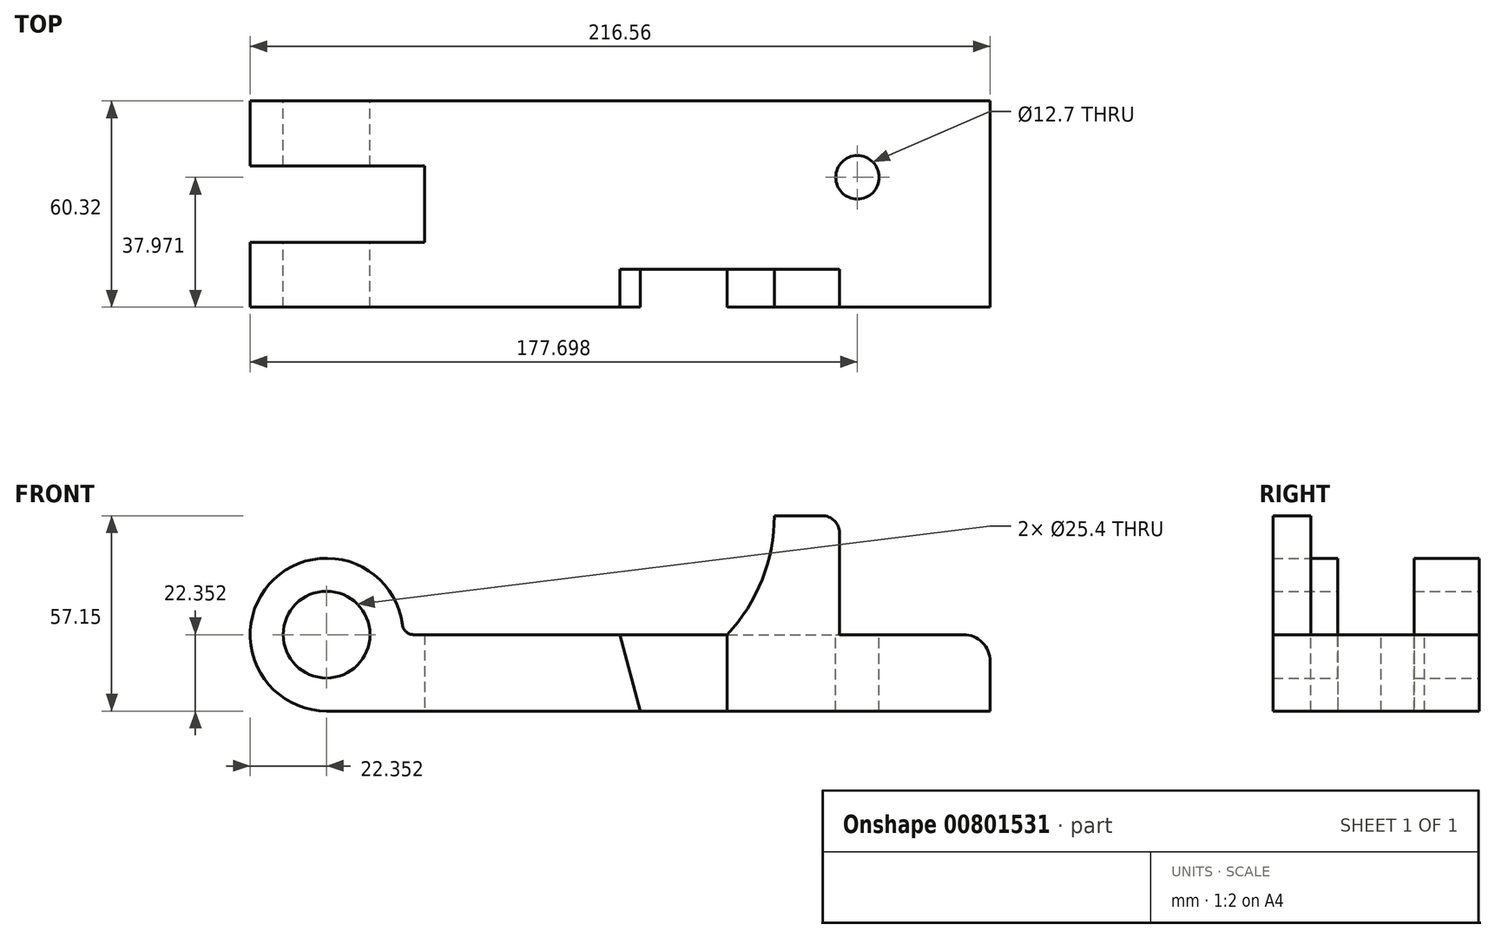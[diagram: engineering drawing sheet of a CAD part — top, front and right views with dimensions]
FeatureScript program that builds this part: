
annotation { "Feature Type Name" : "Feature", "Feature Type Description" : "" }
export const myFeature = defineFeature(function(context is Context, id is Id, definition is map)
    precondition{}
    {
        {
            var Q0;
            Q0=qCreatedBy(makeId("Front.planeOp"),FACE);
            var sketch = newSketch(context, id + "F0", { "sketchPlane" : qUnion([Q0])});
            skLineSegment(sketch, "E0.bottom", {"start": v(0, 0) * mm, "end": v(-194.2, 0) * mm});
            skLineSegment(sketch, "E0.top", {"start": v(-49.2, 57.15) * mm, "end": v(-63.17, 57.15) * mm});
            skLineSegment(sketch, "E0.left", {"start": v(0, 0) * mm, "end": v(0, 22.35) * mm});
            skLineSegment(sketch, "E1.bottom", {"start": v(-194.2, 0) * mm, "end": v(0, 0) * mm});
            skLineSegment(sketch, "E1.top", {"start": v(-216.56, 22.35) * mm, "end": v(-7.87, 22.35) * mm});
            skLineSegment(sketch, "E1.right", {"start": v(0, 0) * mm, "end": v(0, 14.48) * mm});
            skLineSegment(sketch, "E2", {"start": v(-76.96, 22.35) * mm, "end": v(-76.96, 0) * mm});
            skLineSegment(sketch, "E3", {"start": v(-194.2, 71.24) * mm, "end": v(-194.2, -42.33) * mm, "construction": true});
            skCircle(sketch, "E4", {"center": v(-194.2, 22.35) * mm, "radius": 12.7 * mm});
            skCircle(sketch, "E5", {"center": v(-194.2, 22.35) * mm, "radius": 22.35 * mm});
            skLineSegment(sketch, "E6", {"start": v(-102.36, 0) * mm, "end": v(-108.36, 22.35) * mm});
            skLineSegment(sketch, "E7", {"start": v(-44.12, 22.35) * mm, "end": v(-44.12, 52.07) * mm});
            skLineSegment(sketch, "E8", {"start": v(-63.17, 74.18) * mm, "end": v(-63.17, 57.15) * mm, "construction": true});
            skArc(sketch, "E9", {"start": v(-63.17, 57.15) * mm, "mid": v(-66.74, 38.44) * mm, "end": v(-76.96, 22.35) * mm});
            skPoint(sketch, "E10.visualSharp", {"position": v(0, 22.35) * mm});
            skArc(sketch, "E10.filletArc", {"start": v(0, 14.48) * mm, "mid": v(-2.3, 20.05) * mm, "end": v(-7.87, 22.35) * mm});
            skPoint(sketch, "E11.visualSharp", {"position": v(-44.12, 57.15) * mm});
            skArc(sketch, "E11.filletArc", {"start": v(-44.12, 52.07) * mm, "mid": v(-45.6, 55.66) * mm, "end": v(-49.2, 57.15) * mm});
            skLineSegment(sketch, "E12", {"start": v(-165.93, 22.35) * mm, "end": v(-165.93, 0) * mm});
            skSolve(sketch);
        }
        {
            var Q0;
            {var subQ0=sQuery(id+"F0.wireOp",EDGE,"E5");var subQ1=sQuery(id+"F0.wireOp",EDGE,"E1.top");var subQ2=makeQuery(id+"F0.imprint","INTERSECT",VERTEX,{"disambiguationData":[OD(0.0)],"derivedFrom":[subQ1,subQ0]});Q0=makeQuery(id+"F0.imprint","IMPRINT",FACE,{"disambiguationData":[TD([[makeQuery(id+"F0.imprint","IMPRINT",EDGE,{"disambiguationData":[TD([[subQ2,-1.0]])],"derivedFrom":subQ1}),1.0]])]});}
            var Q1;
            {var subQ0=sQuery(id+"F0.wireOp",EDGE,"E5");var subQ2=sQuery(id+"F0.wireOp",EDGE,"E1.top");var subQ7=makeQuery(id+"F0.imprint","INTERSECT",VERTEX,{"disambiguationData":[OD(0.0)],"derivedFrom":[subQ2,subQ0]});Q1=makeQuery(id+"F0.imprint","IMPRINT",FACE,{"disambiguationData":[TD([[makeQuery(id+"F0.imprint","IMPRINT",EDGE,{"disambiguationData":[TD([[subQ7,-1.0]])],"derivedFrom":subQ2}),-1.0]])]});}
            var Q2;
            {var subQ0=sQuery(id+"F0.wireOp",EDGE,"E6");Q2=makeQuery(id+"F0.imprint","IMPRINT",FACE,{"disambiguationData":[TD([[makeQuery(id+"F0.imprint","IMPRINT",EDGE,{"derivedFrom":subQ0}),1.0]])]});}
            var Q3;
            {var subQ0=sQuery(id+"F0.wireOp",EDGE,"E2");Q3=makeQuery(id+"F0.imprint","IMPRINT",FACE,{"disambiguationData":[TD([[makeQuery(id+"F0.imprint","IMPRINT",EDGE,{"derivedFrom":subQ0}),1.0]])]});}
            var Q4;
            {var subQ2=sQuery(id+"F0.wireOp",EDGE,"E2");Q4=makeQuery(id+"F0.imprint","IMPRINT",FACE,{"disambiguationData":[TD([[makeQuery(id+"F0.imprint","IMPRINT",EDGE,{"derivedFrom":subQ2}),-1.0]])]});}
            var Q5;
            {var subQ0=sQuery(id+"F0.wireOp",EDGE,"E12");Q5=makeQuery(id+"F0.imprint","IMPRINT",FACE,{"disambiguationData":[TD([[makeQuery(id+"F0.imprint","IMPRINT",EDGE,{"derivedFrom":subQ0}),-1.0]])]});}
            extrude(context, id + "F1", {"entities" : qUnion([Q0, Q1, Q2, Q3, Q4, Q5]), "depth" : 60.32 * mm, "offsetDistance" : 25.4 * mm, "symmetric" : true});
        }
        {
            var Q0;
            Q0=makeQuery(id+"F0.imprint","IMPRINT",FACE,{"disambiguationData":[TD([[makeQuery(id+"F0.imprint","IMPRINT",EDGE,{"derivedFrom":sQuery(id+"F0.wireOp",EDGE,"E0.top")}),1.0]])]});
            var Q1;
            Q1=makeQuery(id+"F1.opExtrude","CAP_FACE",FACE,{"disambiguationData":[OSD([sQuery(id+"F0.wireOp",EDGE,"E0.bottom"),sQuery(id+"F0.wireOp",EDGE,"E0.left"),sQuery(id+"F0.wireOp",EDGE,"E1.top"),sQuery(id+"F0.wireOp",EDGE,"E4"),sQuery(id+"F0.wireOp",EDGE,"E5"),sQuery(id+"F0.wireOp",EDGE,"E10.filletArc")])],"isStart":false});
            extrude(context, id + "F2", {"entities" : qUnion([Q0]), "operationType" : NewBodyOperationType.ADD, "endBound" : BoundingType.UP_TO_SURFACE, "depth" : 25.4 * mm, "endBoundEntityFace" : qUnion([Q1]), "offsetDistance" : 25.4 * mm, "offsetOppositeDirection" : true, "hasSecondDirection" : true, "secondDirectionOppositeDirection" : false, "secondDirectionDepth" : 19.05 * mm});
        }
        {
            var Q0;
            {var subQ2=sQuery(id+"F0.wireOp",EDGE,"E2");Q0=makeQuery(id+"F0.imprint","IMPRINT",FACE,{"disambiguationData":[TD([[makeQuery(id+"F0.imprint","IMPRINT",EDGE,{"derivedFrom":subQ2}),-1.0]])]});}
            extrude(context, id + "F3", {"entities" : qUnion([Q0]), "operationType" : NewBodyOperationType.REMOVE, "endBound" : BoundingType.UP_TO_NEXT, "depth" : 25.4 * mm, "offsetDistance" : 25.4 * mm, "hasSecondDirection" : true, "secondDirectionOppositeDirection" : false, "secondDirectionDepth" : 19.05 * mm});
        }
        {
            var Q0;
            Q0=makeQuery(id+"F1.opExtrude","SWEPT_EDGE",EDGE,{"disambiguationData":[OSD([sQuery(id+"F0.wireOp",EDGE,"E1.top"),sQuery(id+"F0.wireOp",EDGE,"E5")])]});
            fillet(context, id + "F4", {"entities" : qUnion([Q0]), "radius" : 3.3 * mm, "tangentPropagation" : true, "allowEdgeOverflow" : false});
        }
        {
            var Q0;
            Q0=qCreatedBy(makeId("Top.planeOp"),FACE);
            var sketch = newSketch(context, id + "F5", { "sketchPlane" : qUnion([Q0])});
            skLineSegment(sketch, "E13", {"start": v(-165.45, 0) * mm, "end": v(-165.45, -11.16) * mm});
            skLineSegment(sketch, "E14", {"start": v(-165.45, -11.16) * mm, "end": v(-218.3, -11.16) * mm});
            skLineSegment(sketch, "E15", {"start": v(-218.3, -11.16) * mm, "end": v(-218.3, 11.16) * mm});
            skLineSegment(sketch, "E16", {"start": v(-218.3, 11.16) * mm, "end": v(-165.45, 11.16) * mm});
            skLineSegment(sketch, "E17", {"start": v(-165.45, 11.16) * mm, "end": v(-165.45, 0) * mm});
            skSolve(sketch);
        }
        {
            var Q0;
            Q0=qSketchRegion(id+"F5",true);
            extrude(context, id + "F6", {"entities" : qUnion([Q0]), "operationType" : NewBodyOperationType.REMOVE, "endBound" : BoundingType.THROUGH_ALL, "depth" : 25.4 * mm, "offsetDistance" : 25.4 * mm});
        }
        {
            var Q0;
            Q0=makeQuery(id+"F1.opExtrude","SWEPT_FACE",FACE,{"disambiguationData":[OSD([sQuery(id+"F0.wireOp",EDGE,"E1.top")])]});
            var sketch = newSketch(context, id + "F7", { "sketchPlane" : qUnion([Q0])});
            skCircle(sketch, "E18", {"center": v(-38.86, 7.81) * mm, "radius": 6.35 * mm});
            skSolve(sketch);
        }
        {
            var Q0;
            Q0=qSketchRegion(id+"F7",true);
            extrude(context, id + "F8", {"entities" : qUnion([Q0]), "operationType" : NewBodyOperationType.REMOVE, "endBound" : BoundingType.THROUGH_ALL, "oppositeDirection" : true, "depth" : 25.4 * mm, "offsetDistance" : 25.4 * mm});
        }
    });
